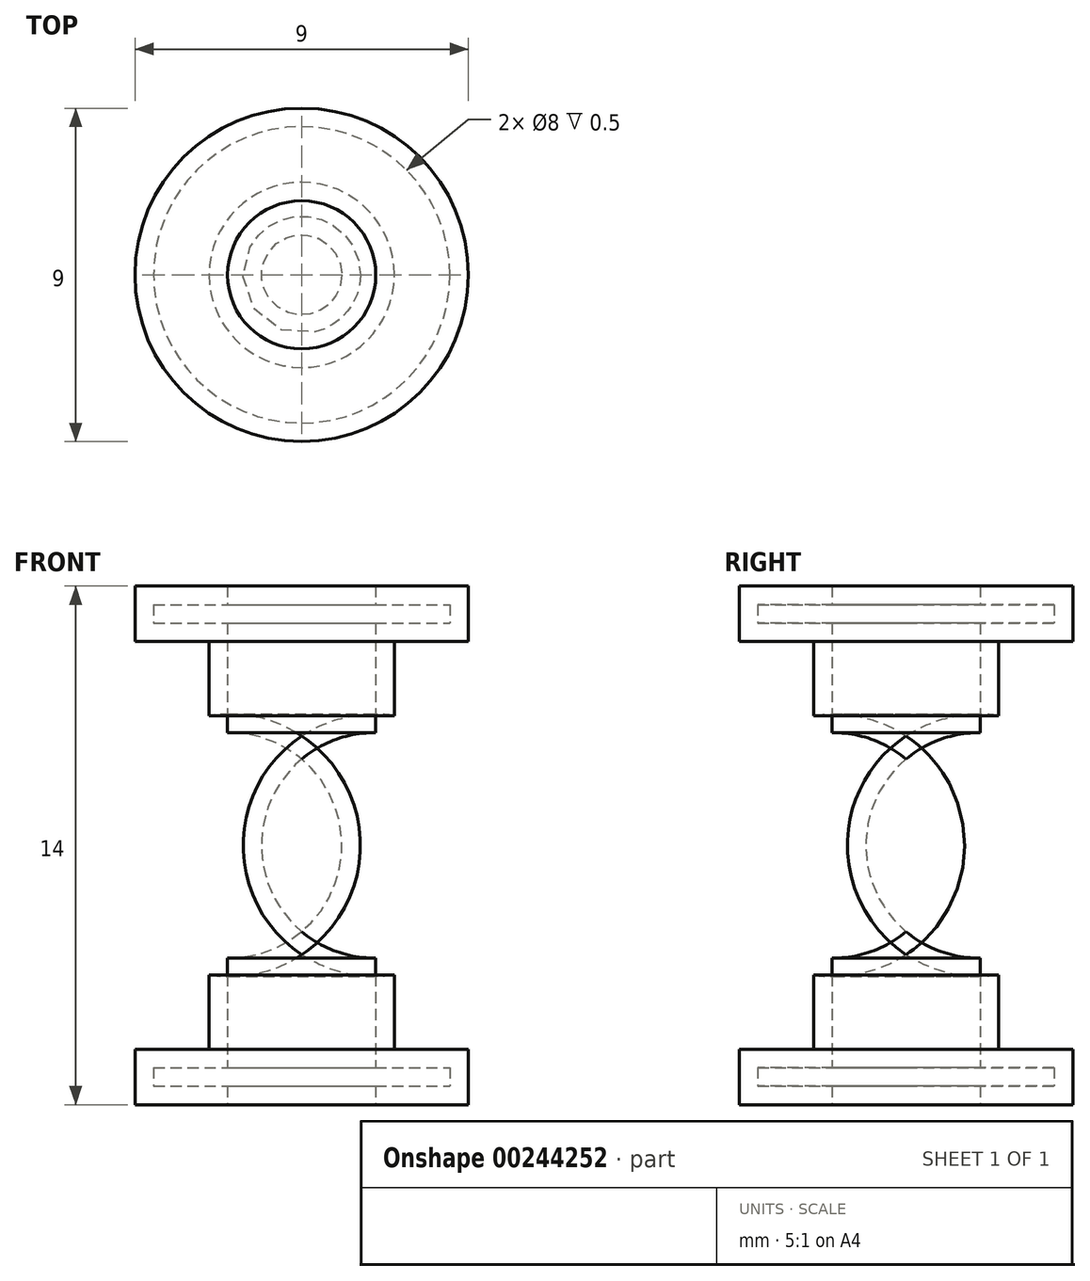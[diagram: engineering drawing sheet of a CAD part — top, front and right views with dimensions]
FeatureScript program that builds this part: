
annotation { "Feature Type Name" : "Feature", "Feature Type Description" : "" }
export const myFeature = defineFeature(function(context is Context, id is Id, definition is map)
    precondition{}
    {
        {
            var Q0;
            Q0=qCreatedBy(makeId("Front.planeOp"),FACE);
            var sketch = newSketch(context, id + "F0", { "sketchPlane" : qUnion([Q0])});
            skLineSegment(sketch, "E0", {"start": v(0, 0) * mm, "end": v(0, 14) * mm, "construction": true});
            skLineSegment(sketch, "E1", {"start": v(0, 7) * mm, "end": v(5.5, 7) * mm, "construction": true});
            skLineSegment(sketch, "E2", {"start": v(0, 1.5) * mm, "end": v(2.5, 1.5) * mm, "construction": true});
            skLineSegment(sketch, "E3", {"start": v(2, 0) * mm, "end": v(4.5, 0) * mm});
            skLineSegment(sketch, "E4", {"start": v(4.5, 0) * mm, "end": v(4.5, 1.5) * mm});
            skLineSegment(sketch, "E5", {"start": v(4.5, 1.5) * mm, "end": v(2.5, 1.5) * mm});
            skLineSegment(sketch, "E6", {"start": v(2.5, 1.5) * mm, "end": v(2.5, 3.5) * mm});
            skLineSegment(sketch, "E7", {"start": v(2, 14) * mm, "end": v(4.5, 14) * mm});
            skLineSegment(sketch, "E8", {"start": v(4.5, 14) * mm, "end": v(4.5, 12.5) * mm});
            skLineSegment(sketch, "E9", {"start": v(4.5, 12.5) * mm, "end": v(2.5, 12.5) * mm});
            skLineSegment(sketch, "E10", {"start": v(2.5, 12.5) * mm, "end": v(2.5, 10.5) * mm});
            skArc(sketch, "E11", {"start": v(2.5, 3.5) * mm, "mid": v(5.5, 7) * mm, "end": v(2.5, 10.5) * mm});
            skLineSegment(sketch, "E12.0", {"start": v(2, 0.5) * mm, "end": v(4, 0.5) * mm});
            skLineSegment(sketch, "E12.1", {"start": v(4, 0.5) * mm, "end": v(4, 1) * mm});
            skLineSegment(sketch, "E12.2", {"start": v(4, 1) * mm, "end": v(2, 1) * mm});
            skLineSegment(sketch, "E12.3", {"start": v(2, 1) * mm, "end": v(2, 3.96) * mm});
            skArc(sketch, "E12.4", {"start": v(2, 3.96) * mm, "mid": v(5, 7) * mm, "end": v(2, 10.04) * mm});
            skLineSegment(sketch, "E12.5", {"start": v(2, 13.5) * mm, "end": v(4, 13.5) * mm});
            skLineSegment(sketch, "E12.6", {"start": v(4, 13.5) * mm, "end": v(4, 13) * mm});
            skLineSegment(sketch, "E12.7", {"start": v(4, 13) * mm, "end": v(2, 13) * mm});
            skLineSegment(sketch, "E12.8", {"start": v(2, 13) * mm, "end": v(2, 10.04) * mm});
            skLineSegment(sketch, "E13", {"start": v(2, 13.5) * mm, "end": v(2, 14) * mm});
            skPoint(sketch, "E14.orphan", {"position": v(0, 13.5) * mm});
            skLineSegment(sketch, "E15", {"start": v(2, 0.5) * mm, "end": v(2, 0) * mm});
            skPoint(sketch, "E16.orphan", {"position": v(0, 0.5) * mm});
            skSolve(sketch);
        }
        {
            var Q0;
            Q0=qSketchRegion(id+"F0",true);
            var Q1;
            Q1=sQuery(id+"F0.wireOp",EDGE,"E0");
            revolve(context, id + "F1", {"entities" : qUnion([Q0]), "axis" : qUnion([Q1]), "revolveType" : RevolveType.FULL});
        }
    });
